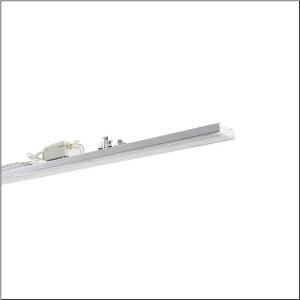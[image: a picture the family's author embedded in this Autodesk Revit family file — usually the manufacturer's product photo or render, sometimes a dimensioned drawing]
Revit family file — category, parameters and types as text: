
# Revit family: licross_21_recessed_mo_52te12cn49xg
name_source: partatom
category: Lighting Fixtures
units: mm (PartAtom-declared; Revit-internal decimal feet)

## family parameters
Cut with Voids When Loaded = No
Host = Face
Light Source = No
Part Type = Normal
Room Calculation Point = No
Round Connector Dimension = Use Diameter
Shared = No

## types (1)
- --- (1 x LED, 9260 lm, 49.9 W, 4000K)
    Apparent Load = 50 VA
    CIE Flux Codes = 72 92 99 100 100
    Color Rendering = 80
    Color Temperature = 4000K
    Default Elevation = 1800 mm
    Description = Licross 21 Recessed MO, luminaire insert, of sheet steel, galvanised, coil coated, white, length: 1.500mm, width: 66mm, height: 67mm, LED rated luminous flux: 9.260lm, light colour: 840, SDCM (Standard Deviation of Colour Matching)MacAdam ≤ 3 SDCM (initial), control gear: ON/OFF Multilumen, CLOi, with plug, 3-pole, with phase selection, mains connection: 220..240V, AC, 50/60Hz, start of lifetime: 49W, end of service life: 61W, internal wiring halogen-free, primary optical cover: cover, of PMMA, light emission: direct distribution, primary light characteristic: symmetric, protection rating (complete): IP54, insulation class (complete): insulation class I (protective earthing), certification: CE, ENEC, VDE, UKCA, protection symbol: D if used in an environment with non-conductive dust loads with corresponding accessories, impact resistance: IK06, permissible ambient temperature for indoor applications: -35..+40°C, corresponds to IFS (International Featured Standards) requirements for safety and quality in the food industry, reducing of maximum allowable ambient temperature of 5°C with ceiling mounting, LABS conformity tested according to VDMA 24364:2018-05, The light source and the operating device comply with the requirements of the Ecodesign Regulation (EU) 2019/2020 and are replaceable in accordance with this regulation, packaging unit: 1 piece
    Height = 58 mm
    Lamp = 1 x LED
    Lamp Light Flux = 9260 lm
    Lamp Power = 49.9 W
    Lamp count = 1
    Length = 1500 mm
    Luminous efficacy = 186 lm/W
    Manufacturer = Siteco
    ModVariant = No
    Model = 52TE12CN49XG
    Mounting Place = Ceiling
    Mounting Type = Pendant
    Number of Poles = 1
    OnlyDefault = Yes
    Power Factor = 1
    Product Name = Licross 21 Recessed MO
    Product group = luminaire insert | ceiling pendant
    ProductGroupID = 901
    Protection Class = Protection class I
    Protection Degree = IP 54
    RLX_Detail_Level = 1
    RLX_Emergency_Light_Flux = 0 lm
    RLX_Emergency_Type = 0
    RLX_Emergency_Type_DB = No
    RlxData = <blob elided: 22593 chars, md5=ea786e26>
    Socket = socket
    Standby Power = 0 W
    System Light Flux = 9260 lm
    System Power = 50 W
    Type Comments = factory setting: luminous flux: 100 % | (A | C | E) | 116 mA
    Type Image = l_1296930.jpg
    URL = http://relux.com
    VarID = @adj_112081
    Voltage = 0 V
    Weight = 0.00 kg
    Width = 66 mm

## geometry (parser evidence)
native form markers: Blend x4, Sweep x13
no freeform markers — native parametric forms only
